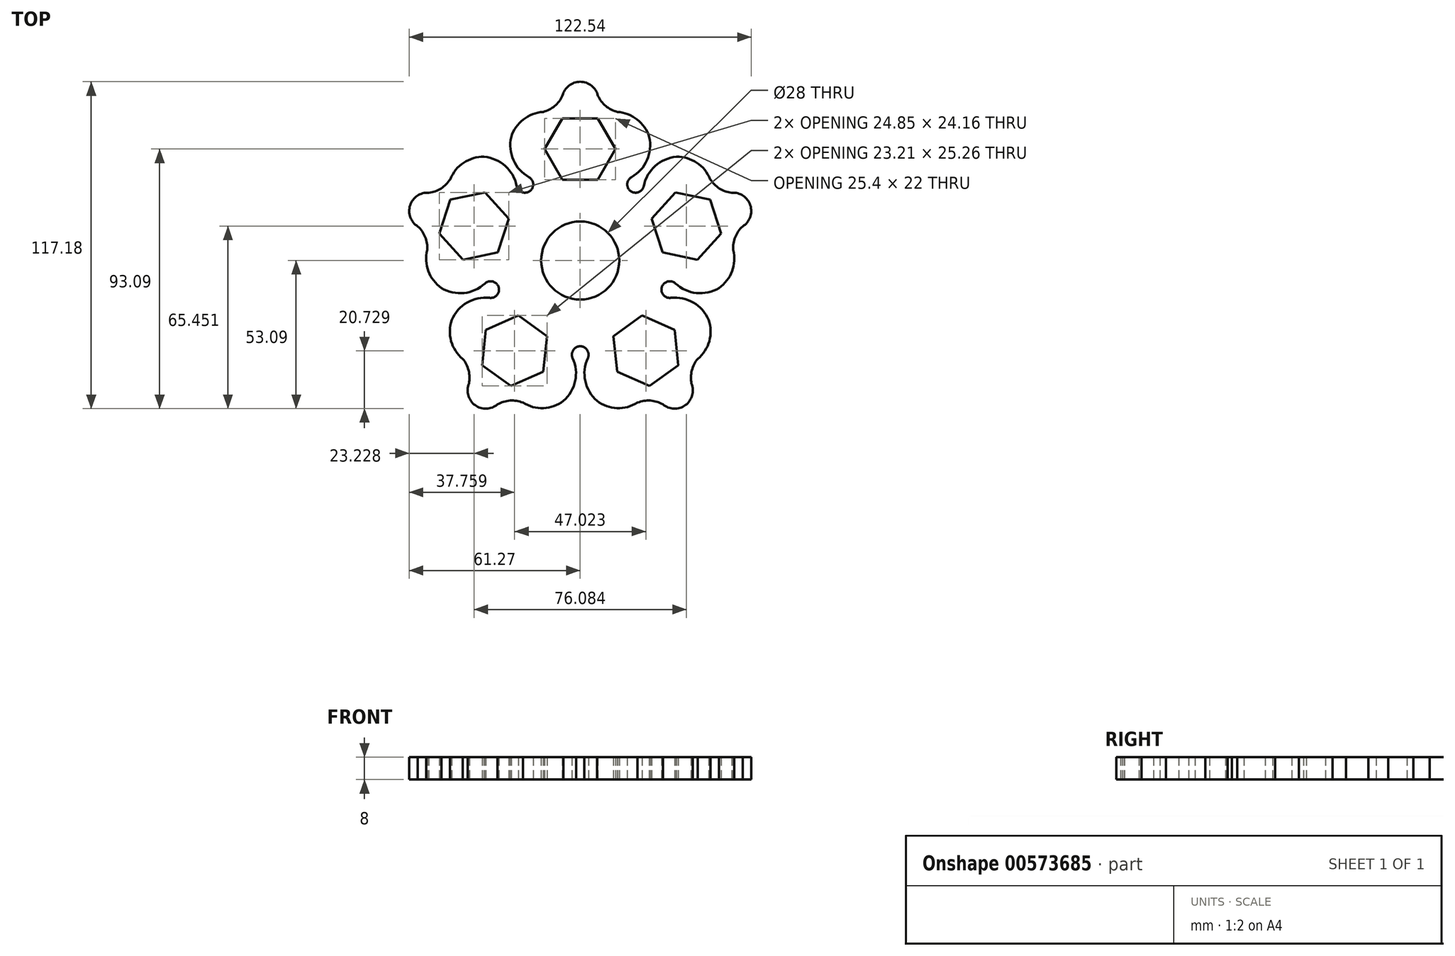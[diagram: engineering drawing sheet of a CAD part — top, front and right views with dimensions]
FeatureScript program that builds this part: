
annotation { "Feature Type Name" : "Feature", "Feature Type Description" : "" }
export const myFeature = defineFeature(function(context is Context, id is Id, definition is map)
    precondition{}
    {
        {
            var Q0;
            Q0=qCreatedBy(makeId("Top.planeOp"),FACE);
            var sketch = newSketch(context, id + "F0", { "sketchPlane" : qUnion([Q0])});
            skCircle(sketch, "E0", {"center": v(0, 0) * mm, "radius": 14 * mm});
            skLineSegment(sketch, "E1", {"start": v(0, 0) * mm, "end": v(0, 40) * mm});
            skLineSegment(sketch, "E2.0", {"start": v(6.35, 51) * mm, "end": v(12.7, 40) * mm});
            skLineSegment(sketch, "E2.1", {"start": v(12.7, 40) * mm, "end": v(6.35, 29) * mm});
            skLineSegment(sketch, "E2.2", {"start": v(6.35, 29) * mm, "end": v(-6.35, 29) * mm});
            skLineSegment(sketch, "E2.3", {"start": v(-6.35, 29) * mm, "end": v(-12.7, 40) * mm});
            skLineSegment(sketch, "E2.4", {"start": v(-12.7, 40) * mm, "end": v(-6.35, 51) * mm});
            skLineSegment(sketch, "E2.5", {"start": v(-6.35, 51) * mm, "end": v(6.35, 51) * mm});
            skPoint(sketch, "E2.0.midPoint", {"position": v(9.53, 45.5) * mm});
            skLineSegment(sketch, "E3.1.0", {"start": v(-41.97, 0.28) * mm, "end": v(-50.47, 9.72) * mm});
            skPoint(sketch, "E3.1.1", {"position": v(-40.33, 23.12) * mm});
            skLineSegment(sketch, "E3.1.2", {"start": v(-29.54, 2.92) * mm, "end": v(-41.97, 0.28) * mm});
            skLineSegment(sketch, "E3.1.3", {"start": v(-34.12, 24.44) * mm, "end": v(-25.62, 15) * mm});
            skLineSegment(sketch, "E3.1.5", {"start": v(-50.47, 9.72) * mm, "end": v(-46.54, 21.8) * mm});
            skLineSegment(sketch, "E3.1.6", {"start": v(-25.62, 15) * mm, "end": v(-29.54, 2.92) * mm});
            skLineSegment(sketch, "E3.1.7", {"start": v(-46.54, 21.8) * mm, "end": v(-34.12, 24.44) * mm});
            skLineSegment(sketch, "E3.2.0", {"start": v(-13.24, -39.83) * mm, "end": v(-24.84, -45) * mm});
            skPoint(sketch, "E3.2.1", {"position": v(-34.45, -31.21) * mm});
            skLineSegment(sketch, "E3.2.2", {"start": v(-11.9, -27.2) * mm, "end": v(-13.24, -39.83) * mm});
            skLineSegment(sketch, "E3.2.3", {"start": v(-33.79, -24.9) * mm, "end": v(-22.18, -19.73) * mm});
            skLineSegment(sketch, "E3.2.5", {"start": v(-24.84, -45) * mm, "end": v(-35.11, -37.53) * mm});
            skLineSegment(sketch, "E3.2.6", {"start": v(-22.18, -19.73) * mm, "end": v(-11.9, -27.2) * mm});
            skLineSegment(sketch, "E3.2.7", {"start": v(-35.11, -37.53) * mm, "end": v(-33.79, -24.9) * mm});
            skLineSegment(sketch, "E3.3.0", {"start": v(33.79, -24.9) * mm, "end": v(35.11, -37.53) * mm});
            skPoint(sketch, "E3.3.1", {"position": v(19.04, -42.4) * mm});
            skLineSegment(sketch, "E3.3.2", {"start": v(22.18, -19.73) * mm, "end": v(33.79, -24.9) * mm});
            skLineSegment(sketch, "E3.3.3", {"start": v(13.24, -39.83) * mm, "end": v(11.9, -27.2) * mm});
            skLineSegment(sketch, "E3.3.5", {"start": v(35.11, -37.53) * mm, "end": v(24.84, -45) * mm});
            skLineSegment(sketch, "E3.3.6", {"start": v(11.9, -27.2) * mm, "end": v(22.18, -19.73) * mm});
            skLineSegment(sketch, "E3.3.7", {"start": v(24.84, -45) * mm, "end": v(13.24, -39.83) * mm});
            skLineSegment(sketch, "E3.4.0", {"start": v(34.12, 24.44) * mm, "end": v(46.54, 21.8) * mm});
            skPoint(sketch, "E3.4.1", {"position": v(46.22, 5) * mm});
            skLineSegment(sketch, "E3.4.2", {"start": v(25.62, 15) * mm, "end": v(34.12, 24.44) * mm});
            skLineSegment(sketch, "E3.4.3", {"start": v(41.97, 0.28) * mm, "end": v(29.54, 2.92) * mm});
            skLineSegment(sketch, "E3.4.5", {"start": v(46.54, 21.8) * mm, "end": v(50.47, 9.72) * mm});
            skLineSegment(sketch, "E3.4.6", {"start": v(29.54, 2.92) * mm, "end": v(25.62, 15) * mm});
            skLineSegment(sketch, "E3.4.7", {"start": v(50.47, 9.72) * mm, "end": v(41.97, 0.28) * mm});
            skLineSegment(sketch, "E4", {"start": v(0, 0) * mm, "end": v(0, 71.56) * mm});
            skPoint(sketch, "E4.endSnap0", {"position": v(0, 51) * mm});
            skArc(sketch, "E5", {"start": v(-24.72, 44.26) * mm, "mid": v(-23.81, 35.73) * mm, "end": v(-17.82, 29.6) * mm});
            skArc(sketch, "E6", {"start": v(-13.33, 53.29) * mm, "mid": v(-20.44, 50.56) * mm, "end": v(-24.72, 44.26) * mm});
            skArc(sketch, "E7", {"start": v(-13.33, 53.29) * mm, "mid": v(-9.18, 55.4) * mm, "end": v(-6.35, 59.1) * mm});
            skArc(sketch, "E8", {"start": v(0, 64.09) * mm, "mid": v(-4.03, 62.7) * mm, "end": v(-6.35, 59.1) * mm});
            skArc(sketch, "E9.MirrorCS", {"start": v(0, 64.09) * mm, "mid": v(4.03, 62.7) * mm, "end": v(6.35, 59.1) * mm});
            skArc(sketch, "E10.MirrorCS", {"start": v(13.33, 53.29) * mm, "mid": v(9.18, 55.4) * mm, "end": v(6.35, 59.1) * mm});
            skArc(sketch, "E11.MirrorCS", {"start": v(13.33, 53.29) * mm, "mid": v(20.44, 50.56) * mm, "end": v(24.72, 44.26) * mm});
            skArc(sketch, "E12.MirrorCS", {"start": v(24.72, 44.26) * mm, "mid": v(23.81, 35.73) * mm, "end": v(17.82, 29.6) * mm});
            skArc(sketch, "E13.1.0", {"start": v(-49.73, -9.83) * mm, "mid": v(-41.34, -11.6) * mm, "end": v(-33.66, -7.8) * mm});
            skArc(sketch, "E13.1.1", {"start": v(-54.8, 3.79) * mm, "mid": v(-54.4, -3.82) * mm, "end": v(-49.73, -9.83) * mm});
            skArc(sketch, "E13.1.2", {"start": v(-54.8, 3.79) * mm, "mid": v(-55.53, 8.4) * mm, "end": v(-58.18, 12.23) * mm});
            skArc(sketch, "E13.1.3", {"start": v(-60.95, 19.8) * mm, "mid": v(-60.87, 15.54) * mm, "end": v(-58.18, 12.23) * mm});
            skArc(sketch, "E13.1.4", {"start": v(-60.95, 19.8) * mm, "mid": v(-58.38, 23.2) * mm, "end": v(-54.25, 24.3) * mm});
            skArc(sketch, "E13.1.5", {"start": v(-46.56, 29.15) * mm, "mid": v(-49.85, 25.85) * mm, "end": v(-54.25, 24.3) * mm});
            skArc(sketch, "E13.1.6", {"start": v(-46.56, 29.15) * mm, "mid": v(-41.77, 35.07) * mm, "end": v(-34.45, 37.18) * mm});
            skArc(sketch, "E13.1.7", {"start": v(-34.45, 37.18) * mm, "mid": v(-26.63, 33.69) * mm, "end": v(-22.64, 26.1) * mm});
            skArc(sketch, "E13.2.0", {"start": v(-6.02, -50.33) * mm, "mid": v(-1.74, -42.9) * mm, "end": v(-2.98, -34.42) * mm});
            skArc(sketch, "E13.2.1", {"start": v(-20.53, -50.95) * mm, "mid": v(-13.18, -52.92) * mm, "end": v(-6.02, -50.33) * mm});
            skArc(sketch, "E13.2.2", {"start": v(-20.53, -50.95) * mm, "mid": v(-25.14, -50.22) * mm, "end": v(-29.6, -51.55) * mm});
            skArc(sketch, "E13.2.3", {"start": v(-37.67, -51.85) * mm, "mid": v(-33.59, -53.09) * mm, "end": v(-29.6, -51.55) * mm});
            skArc(sketch, "E13.2.4", {"start": v(-37.67, -51.85) * mm, "mid": v(-40.11, -48.35) * mm, "end": v(-39.88, -44.09) * mm});
            skArc(sketch, "E13.2.5", {"start": v(-42.1, -35.27) * mm, "mid": v(-40, -39.43) * mm, "end": v(-39.88, -44.09) * mm});
            skArc(sketch, "E13.2.6", {"start": v(-42.1, -35.27) * mm, "mid": v(-46.26, -28.89) * mm, "end": v(-46.01, -21.28) * mm});
            skArc(sketch, "E13.2.7", {"start": v(-46.01, -21.28) * mm, "mid": v(-40.27, -14.91) * mm, "end": v(-31.81, -13.47) * mm});
            skArc(sketch, "E13.3.0", {"start": v(46.01, -21.28) * mm, "mid": v(40.27, -14.91) * mm, "end": v(31.81, -13.47) * mm});
            skArc(sketch, "E13.3.1", {"start": v(42.1, -35.27) * mm, "mid": v(46.26, -28.89) * mm, "end": v(46.01, -21.28) * mm});
            skArc(sketch, "E13.3.2", {"start": v(42.1, -35.27) * mm, "mid": v(40, -39.43) * mm, "end": v(39.88, -44.09) * mm});
            skArc(sketch, "E13.3.3", {"start": v(37.67, -51.85) * mm, "mid": v(40.11, -48.35) * mm, "end": v(39.88, -44.09) * mm});
            skArc(sketch, "E13.3.4", {"start": v(37.67, -51.85) * mm, "mid": v(33.59, -53.09) * mm, "end": v(29.6, -51.55) * mm});
            skArc(sketch, "E13.3.5", {"start": v(20.53, -50.95) * mm, "mid": v(25.14, -50.22) * mm, "end": v(29.6, -51.55) * mm});
            skArc(sketch, "E13.3.6", {"start": v(20.53, -50.95) * mm, "mid": v(13.18, -52.92) * mm, "end": v(6.02, -50.33) * mm});
            skArc(sketch, "E13.3.7", {"start": v(6.02, -50.33) * mm, "mid": v(1.74, -42.9) * mm, "end": v(2.98, -34.42) * mm});
            skArc(sketch, "E13.4.0", {"start": v(34.45, 37.18) * mm, "mid": v(26.63, 33.69) * mm, "end": v(22.64, 26.1) * mm});
            skArc(sketch, "E13.4.1", {"start": v(46.56, 29.15) * mm, "mid": v(41.77, 35.07) * mm, "end": v(34.45, 37.18) * mm});
            skArc(sketch, "E13.4.2", {"start": v(46.56, 29.15) * mm, "mid": v(49.85, 25.85) * mm, "end": v(54.25, 24.3) * mm});
            skArc(sketch, "E13.4.3", {"start": v(60.95, 19.8) * mm, "mid": v(58.38, 23.2) * mm, "end": v(54.25, 24.3) * mm});
            skArc(sketch, "E13.4.4", {"start": v(60.95, 19.8) * mm, "mid": v(60.87, 15.54) * mm, "end": v(58.18, 12.23) * mm});
            skArc(sketch, "E13.4.5", {"start": v(54.8, 3.79) * mm, "mid": v(55.53, 8.4) * mm, "end": v(58.18, 12.23) * mm});
            skArc(sketch, "E13.4.6", {"start": v(54.8, 3.79) * mm, "mid": v(54.4, -3.82) * mm, "end": v(49.73, -9.83) * mm});
            skArc(sketch, "E13.4.7", {"start": v(49.73, -9.83) * mm, "mid": v(41.34, -11.6) * mm, "end": v(33.66, -7.8) * mm});
            skArc(sketch, "E14", {"start": v(-22.75, 26.7) * mm, "mid": v(-18.07, 24.88) * mm, "end": v(-18.37, 29.9) * mm});
            skArc(sketch, "E15.1.0", {"start": v(-32.43, -13.39) * mm, "mid": v(-29.24, -9.5) * mm, "end": v(-34.1, -8.23) * mm});
            skArc(sketch, "E15.2.0", {"start": v(2.7, -34.98) * mm, "mid": v(0, -30.75) * mm, "end": v(-2.7, -34.98) * mm});
            skArc(sketch, "E15.3.0", {"start": v(34.1, -8.23) * mm, "mid": v(29.24, -9.5) * mm, "end": v(32.43, -13.39) * mm});
            skArc(sketch, "E15.4.0", {"start": v(18.37, 29.9) * mm, "mid": v(18.07, 24.88) * mm, "end": v(22.75, 26.7) * mm});
            skSolve(sketch);
        }
        {
            var Q0;
            Q0 = qSketchRegion(id + "F0", true);
            extrude(context, id + "F1", {"entities" : qUnion([Q0]), "depth" : 8 * mm, "offsetDistance" : 25 * mm});
        }
    });
